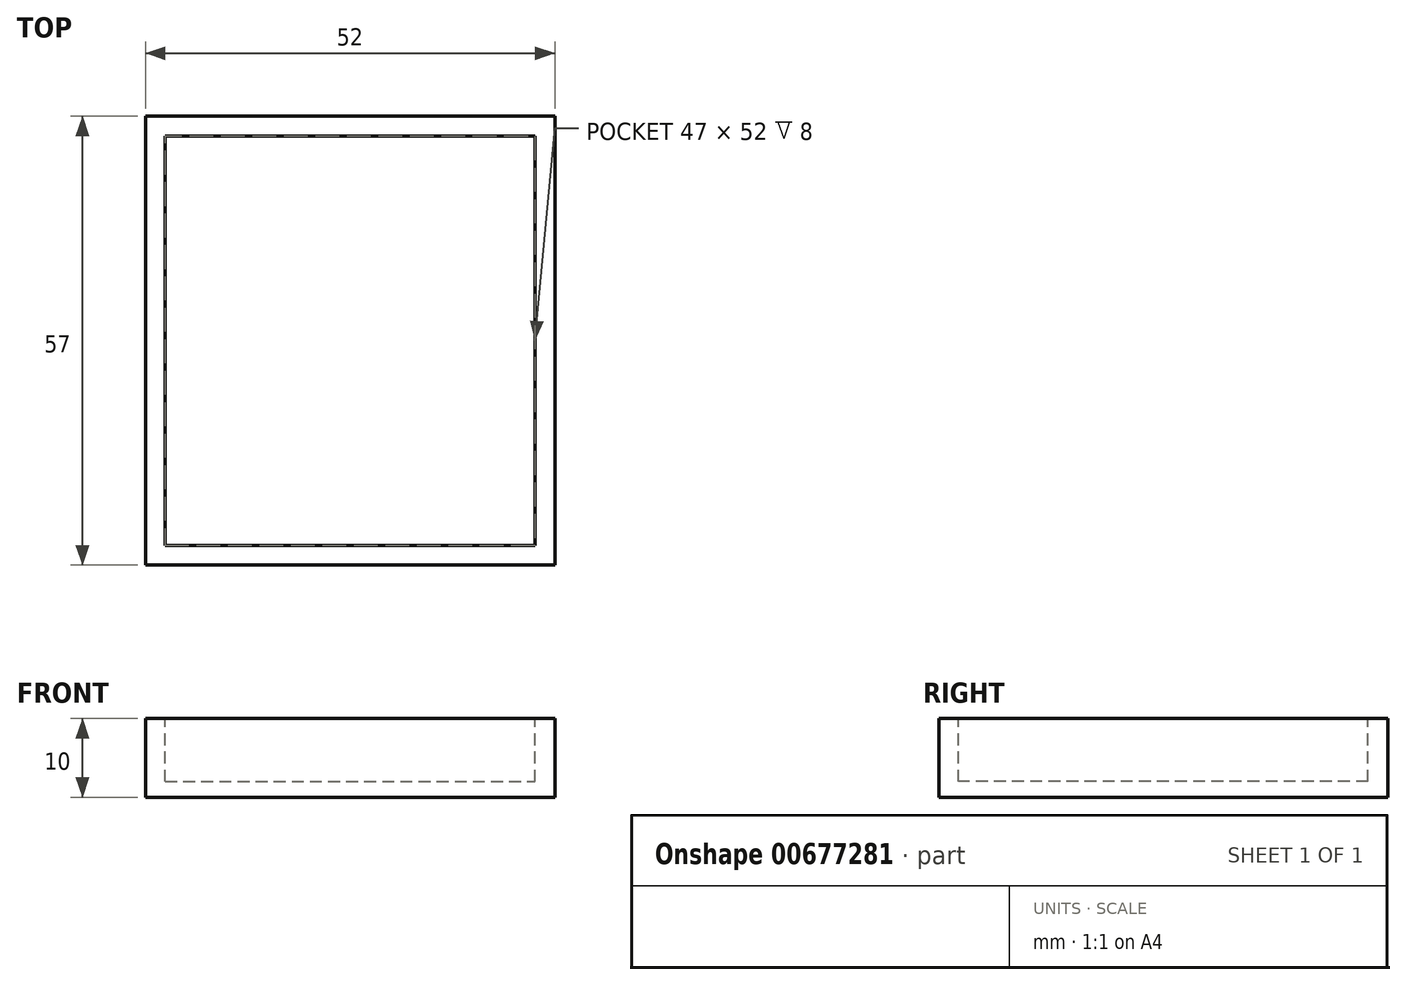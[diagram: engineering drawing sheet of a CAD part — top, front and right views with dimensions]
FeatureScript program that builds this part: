
annotation { "Feature Type Name" : "Feature", "Feature Type Description" : "" }
export const myFeature = defineFeature(function(context is Context, id is Id, definition is map)
    precondition{}
    {
        {
            var Q0;
            Q0=qCreatedBy(makeId("Top.planeOp"),FACE);
            var sketch = newSketch(context, id + "F0", { "sketchPlane" : qUnion([Q0])});
            skLineSegment(sketch, "E0.bottom", {"start": v(-26, 28.5) * mm, "end": v(26, 28.5) * mm});
            skLineSegment(sketch, "E0.top", {"start": v(-26, -28.5) * mm, "end": v(26, -28.5) * mm});
            skLineSegment(sketch, "E0.left", {"start": v(-26, 28.5) * mm, "end": v(-26, -28.5) * mm});
            skLineSegment(sketch, "E0.right", {"start": v(26, 28.5) * mm, "end": v(26, -28.5) * mm});
            skPoint(sketch, "E0.middle", {"position": v(0, 0) * mm});
            skSolve(sketch);
        }
        {
            var Q0;
            Q0 = qSketchRegion(id + "F0", true);
            extrude(context, id + "F1", {"entities" : qUnion([Q0]), "depth" : 10 * mm, "offsetDistance" : 25 * mm});
        }
        {
            var Q0;
            Q0=makeQuery(id+"F1.opExtrude","CAP_FACE",FACE,{"disambiguationData":[OSD([sQuery(id+"F0.wireOp",EDGE,"E0.bottom"),sQuery(id+"F0.wireOp",EDGE,"E0.top"),sQuery(id+"F0.wireOp",EDGE,"E0.left"),sQuery(id+"F0.wireOp",EDGE,"E0.right")])],"isStart":false});
            var sketch = newSketch(context, id + "F2", { "sketchPlane" : qUnion([Q0])});
            skLineSegment(sketch, "E1.bottom", {"start": v(-23.5, 26) * mm, "end": v(23.5, 26) * mm});
            skLineSegment(sketch, "E1.top", {"start": v(-23.5, -26) * mm, "end": v(23.5, -26) * mm});
            skLineSegment(sketch, "E1.left", {"start": v(-23.5, 26) * mm, "end": v(-23.5, -26) * mm});
            skLineSegment(sketch, "E1.right", {"start": v(23.5, 26) * mm, "end": v(23.5, -26) * mm});
            skPoint(sketch, "E1.middle", {"position": v(0, 0) * mm});
            skSolve(sketch);
        }
        {
            var Q0;
            Q0 = qSketchRegion(id + "F2", true);
            extrude(context, id + "F3", {"entities" : qUnion([Q0]), "operationType" : NewBodyOperationType.REMOVE, "depth" : -8 * mm, "offsetDistance" : 25 * mm});
        }
    });
